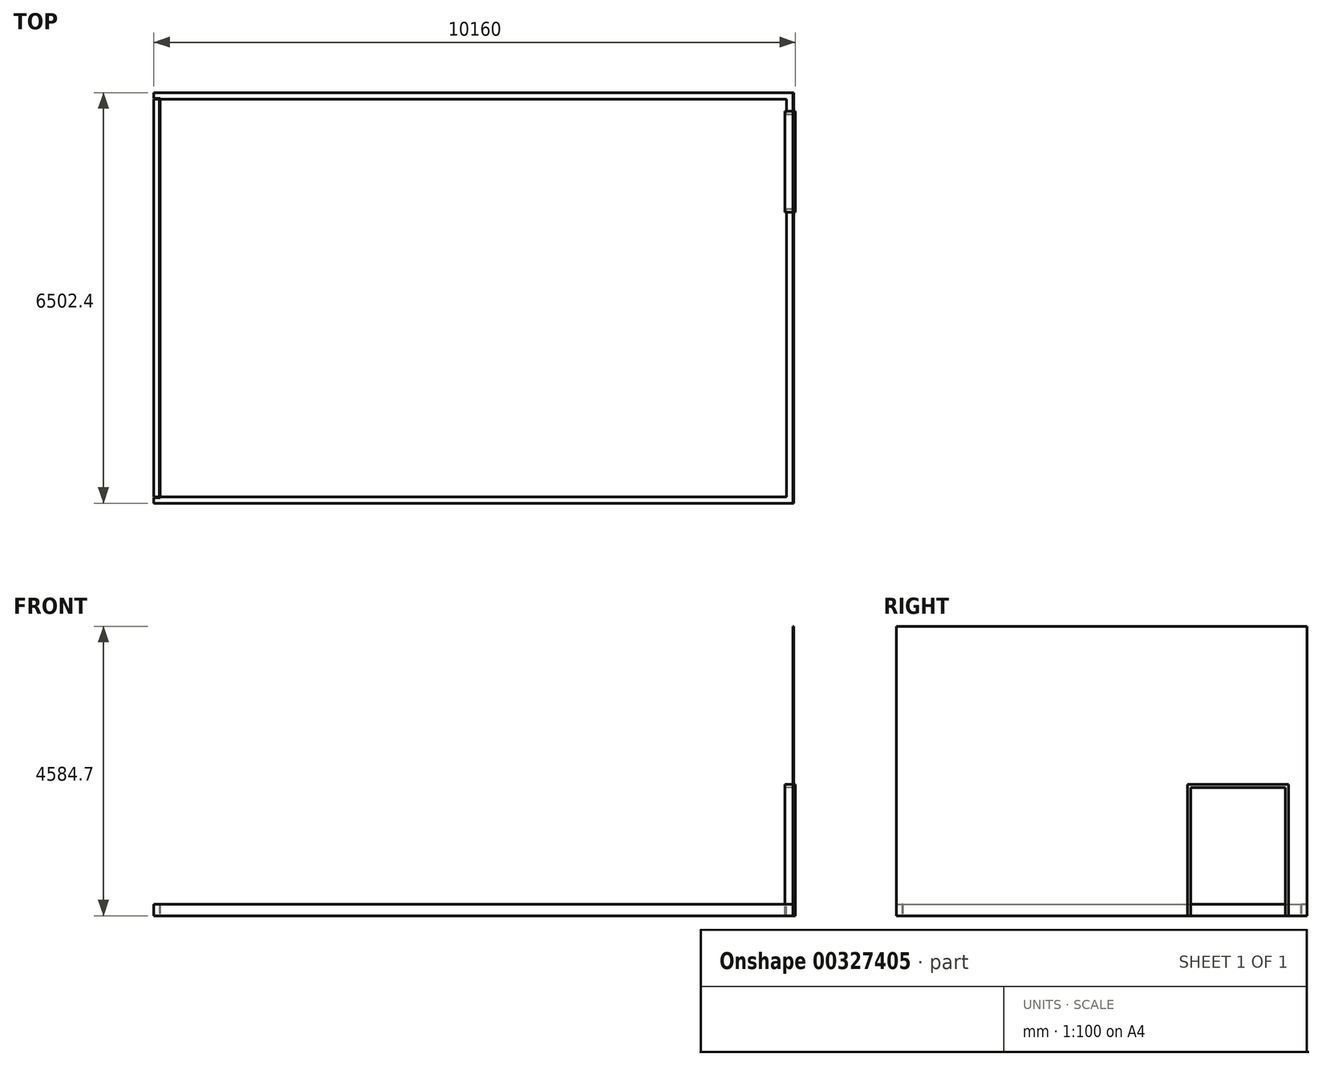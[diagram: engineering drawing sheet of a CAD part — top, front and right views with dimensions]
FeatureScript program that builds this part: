
annotation { "Feature Type Name" : "Feature", "Feature Type Description" : "" }
export const myFeature = defineFeature(function(context is Context, id is Id, definition is map)
    precondition{}
    {
        {
            assignVariable(context, id + "F0", {"name" : "WallHeight", "anyValue" : 15 * 12 + 0.5});
        }
        {
            var Q0;
            Q0=qCreatedBy(makeId("Top.planeOp"),FACE);
            var sketch = newSketch(context, id + "F1", { "sketchPlane" : qUnion([Q0])});
            skLineSegment(sketch, "E0.bottom", {"start": v(0, 6299.2) * mm, "end": v(9918.7, 6299.2) * mm});
            skLineSegment(sketch, "E0.top", {"start": v(0, 0) * mm, "end": v(9918.7, 0) * mm});
            skLineSegment(sketch, "E0.left", {"start": v(0, 6299.2) * mm, "end": v(0, 0) * mm});
            skLineSegment(sketch, "E0.right", {"start": v(9918.7, 6299.2) * mm, "end": v(9918.7, 0) * mm});
            skSolve(sketch);
        }
        {
            var Q0;
            Q0=qCreatedBy(makeId("Top.planeOp"),FACE);
            var sketch = newSketch(context, id + "F2", { "sketchPlane" : qUnion([Q0])});
            skLineSegment(sketch, "E1.bottom", {"start": v(0, 0) * mm, "end": v(-12.7, 0) * mm});
            skLineSegment(sketch, "E1.top", {"start": v(0, 6299.2) * mm, "end": v(-12.7, 6299.2) * mm});
            skLineSegment(sketch, "E1.left", {"start": v(0, 0) * mm, "end": v(0, 6299.2) * mm});
            skLineSegment(sketch, "E1.right", {"start": v(-12.7, 0) * mm, "end": v(-12.7, 6299.2) * mm});
            skSolve(sketch);
        }
        {
            var Q0;
            Q0=makeQuery(id+"F2.imprint","IMPRINT",FACE,{"disambiguationData":[TD([[makeQuery(id+"F2.imprint","IMPRINT",EDGE,{"derivedFrom":sQuery(id+"F2.wireOp",EDGE,"E1.bottom")}),-1.0]])]});
            extrude(context, id + "F3", {"entities" : qUnion([Q0]), "depth" : (getVariable(context, 'WallHeight')) * mm});
        }
        {
            var Q0;
            Q0=qCreatedBy(makeId("Top.planeOp"),FACE);
            var sketch = newSketch(context, id + "F4", { "sketchPlane" : qUnion([Q0])});
            skLineSegment(sketch, "E2.bottom", {"start": v(0, 0) * mm, "end": v(9918.7, 0) * mm});
            skLineSegment(sketch, "E2.top", {"start": v(0, -12.7) * mm, "end": v(9918.7, -12.7) * mm});
            skLineSegment(sketch, "E2.left", {"start": v(0, 0) * mm, "end": v(0, -12.7) * mm});
            skLineSegment(sketch, "E2.right", {"start": v(9918.7, 0) * mm, "end": v(9918.7, -12.7) * mm});
            skSolve(sketch);
        }
        {
            var Q0;
            Q0=qSketchRegion(id+"F4",true);
            extrude(context, id + "F5", {"entities" : qUnion([Q0]), "depth" : (getVariable(context, 'WallHeight')) * mm});
        }
        {
            var Q0;
            Q0=qCreatedBy(makeId("Top.planeOp"),FACE);
            var sketch = newSketch(context, id + "F6", { "sketchPlane" : qUnion([Q0])});
            skLineSegment(sketch, "E3.bottom", {"start": v(9918.7, 0) * mm, "end": v(9931.4, 0) * mm});
            skLineSegment(sketch, "E3.top", {"start": v(9918.7, 6299.2) * mm, "end": v(9931.4, 6299.2) * mm});
            skLineSegment(sketch, "E3.left", {"start": v(9918.7, 0) * mm, "end": v(9918.7, 6299.2) * mm});
            skLineSegment(sketch, "E3.right", {"start": v(9931.4, 0) * mm, "end": v(9931.4, 6299.2) * mm});
            skSolve(sketch);
        }
        {
            var Q0;
            Q0=qSketchRegion(id+"F6",true);
            extrude(context, id + "F7", {"entities" : qUnion([Q0]), "depth" : (getVariable(context, 'WallHeight')) * mm});
        }
        {
            var Q0;
            Q0=qCreatedBy(makeId("Top.planeOp"),FACE);
            var sketch = newSketch(context, id + "F8", { "sketchPlane" : qUnion([Q0])});
            skLineSegment(sketch, "E4.bottom", {"start": v(0, 6299.2) * mm, "end": v(9918.7, 6299.2) * mm});
            skLineSegment(sketch, "E4.top", {"start": v(0, 6311.9) * mm, "end": v(9918.7, 6311.9) * mm});
            skLineSegment(sketch, "E4.left", {"start": v(0, 6299.2) * mm, "end": v(0, 6311.9) * mm});
            skLineSegment(sketch, "E4.right", {"start": v(9918.7, 6299.2) * mm, "end": v(9918.7, 6311.9) * mm});
            skSolve(sketch);
        }
        {
            var Q0;
            Q0=qSketchRegion(id+"F8",true);
            extrude(context, id + "F9", {"entities" : qUnion([Q0]), "depth" : (getVariable(context, 'WallHeight')) * mm});
        }
        {
            var Q0;
            Q0=makeQuery(id+"F3.opExtrude","SWEPT_FACE",FACE,{"disambiguationData":[OSD([sQuery(id+"F2.wireOp",EDGE,"E1.right")])]});
            extrude(context, id + "F10", {"entities" : qUnion([Q0]), "depth" : 88.9 * mm});
        }
        {
            var Q0;
            Q0=makeQuery(id+"F7.opExtrude","SWEPT_FACE",FACE,{"disambiguationData":[OSD([sQuery(id+"F6.wireOp",EDGE,"E3.right")])]});
            extrude(context, id + "F11", {"entities" : qUnion([Q0]), "depth" : 88.9 * mm});
        }
        {
            var Q0;
            Q0=makeQuery(id+"F5.opExtrude","SWEPT_FACE",FACE,{"disambiguationData":[OSD([sQuery(id+"F4.wireOp",EDGE,"E2.top")])]});
            extrude(context, id + "F12", {"entities" : qUnion([Q0]), "depth" : 88.9 * mm});
        }
        {
            var Q0;
            Q0=makeQuery(id+"F12.opExtrude","SWEPT_FACE",FACE,{"disambiguationData":[OSD([sQuery(id+"F4.wireOp",EDGE,"E2.top"),sQuery(id+"F4.wireOp",EDGE,"E2.left")])]});
            extrude(context, id + "F13", {"entities" : qUnion([Q0]), "operationType" : NewBodyOperationType.ADD, "depth" : 101.6 * mm});
        }
        {
            var Q0;
            Q0=makeQuery(id+"F12.opExtrude","SWEPT_FACE",FACE,{"disambiguationData":[OSD([sQuery(id+"F4.wireOp",EDGE,"E2.top"),sQuery(id+"F4.wireOp",EDGE,"E2.right")])]});
            extrude(context, id + "F14", {"entities" : qUnion([Q0]), "operationType" : NewBodyOperationType.ADD, "depth" : 101.6 * mm});
        }
        {
            var Q0;
            Q0=makeQuery(id+"F9.opExtrude","SWEPT_FACE",FACE,{"disambiguationData":[OSD([sQuery(id+"F8.wireOp",EDGE,"E4.top")])]});
            extrude(context, id + "F15", {"entities" : qUnion([Q0]), "depth" : 88.9 * mm});
        }
        {
            var Q0;
            Q0=makeQuery(id+"F15.opExtrude","SWEPT_FACE",FACE,{"disambiguationData":[OSD([sQuery(id+"F8.wireOp",EDGE,"E4.top"),sQuery(id+"F8.wireOp",EDGE,"E4.left")])]});
            extrude(context, id + "F16", {"entities" : qUnion([Q0]), "operationType" : NewBodyOperationType.ADD, "depth" : 101.6 * mm});
        }
        {
            var Q0;
            Q0=makeQuery(id+"F15.opExtrude","SWEPT_FACE",FACE,{"disambiguationData":[OSD([sQuery(id+"F8.wireOp",EDGE,"E4.top"),sQuery(id+"F8.wireOp",EDGE,"E4.right")])]});
            extrude(context, id + "F17", {"entities" : qUnion([Q0]), "operationType" : NewBodyOperationType.ADD, "depth" : 101.6 * mm});
        }
        {
            var Q0;
            Q0=makeQuery(id+"F11.opExtrude","CAP_FACE",FACE,{"disambiguationData":[OSD([sQuery(id+"F6.wireOp",EDGE,"E3.right")])],"isStart":false});
            var sketch = newSketch(context, id + "F18", { "sketchPlane" : qUnion([Q0])});
            skLineSegment(sketch, "E5.bottom", {"start": v(-101.6, 4584.7) * mm, "end": v(6400.8, 4584.7) * mm});
            skLineSegment(sketch, "E5.top", {"start": v(-101.6, 0) * mm, "end": v(6400.8, 0) * mm});
            skLineSegment(sketch, "E5.left", {"start": v(6400.8, 4584.7) * mm, "end": v(6400.8, 0) * mm});
            skLineSegment(sketch, "E5.right", {"start": v(-101.6, 4584.7) * mm, "end": v(-101.6, 0) * mm});
            skSolve(sketch);
        }
        {
            var Q0;
            Q0=qSketchRegion(id+"F18",true);
            extrude(context, id + "F19", {"entities" : qUnion([Q0]), "depth" : 12.7 * mm});
        }
        {
            var Q0;
            Q0=makeQuery(id+"F7.opExtrude","SWEPT_FACE",FACE,{"disambiguationData":[OSD([sQuery(id+"F6.wireOp",EDGE,"E3.left")])]});
            var sketch = newSketch(context, id + "F20", { "sketchPlane" : qUnion([Q0])});
            skLineSegment(sketch, "E6.bottom", {"start": v(-6108.7, 0) * mm, "end": v(-4508.5, 0) * mm});
            skLineSegment(sketch, "E6.top", {"start": v(-6108.7, 2082.8) * mm, "end": v(-4508.5, 2082.8) * mm});
            skLineSegment(sketch, "E6.left", {"start": v(-6108.7, 0) * mm, "end": v(-6108.7, 2082.8) * mm});
            skLineSegment(sketch, "E6.right", {"start": v(-4508.5, 0) * mm, "end": v(-4508.5, 2082.8) * mm});
            skSolve(sketch);
        }
        {
            var Q0;
            Q0=qSketchRegion(id+"F20",true);
            extrude(context, id + "F21", {"entities" : qUnion([Q0]), "depth" : 25.4 * mm, "hasSecondDirection" : true, "secondDirectionOppositeDirection" : true, "secondDirectionDepth" : 139.7 * mm});
        }
        {
            var Q0;
            Q0=makeQuery(id+"F21.opExtrude","CAP_FACE",FACE,{"disambiguationData":[OSD([sQuery(id+"F20.wireOp",EDGE,"E6.bottom"),sQuery(id+"F20.wireOp",EDGE,"E6.top"),sQuery(id+"F20.wireOp",EDGE,"E6.left"),sQuery(id+"F20.wireOp",EDGE,"E6.right")])],"isStart":false});
            var sketch = newSketch(context, id + "F22", { "sketchPlane" : qUnion([Q0])});
            skLineSegment(sketch, "E7.bottom", {"start": v(-6057.9, 0) * mm, "end": v(-4559.3, 0) * mm});
            skLineSegment(sketch, "E7.top", {"start": v(-6057.9, 2032) * mm, "end": v(-4559.3, 2032) * mm});
            skLineSegment(sketch, "E7.left", {"start": v(-6057.9, 0) * mm, "end": v(-6057.9, 2032) * mm});
            skLineSegment(sketch, "E7.right", {"start": v(-4559.3, 0) * mm, "end": v(-4559.3, 2032) * mm});
            skSolve(sketch);
        }
        {
            var Q0;
            Q0=qSketchRegion(id+"F22",true);
            var Q1;
            Q1=makeQuery(id+"F21.opExtrude","CAP_FACE",FACE,{"disambiguationData":[OSD([sQuery(id+"F20.wireOp",EDGE,"E6.bottom"),sQuery(id+"F20.wireOp",EDGE,"E6.top"),sQuery(id+"F20.wireOp",EDGE,"E6.left"),sQuery(id+"F20.wireOp",EDGE,"E6.right")])],"isStart":true});
            extrude(context, id + "F23", {"entities" : qUnion([Q0]), "operationType" : NewBodyOperationType.REMOVE, "endBound" : BoundingType.UP_TO_SURFACE, "oppositeDirection" : true, "endBoundEntityFace" : qUnion([Q1]), "offsetDistance" : 25.4 * mm, "depth" : 25.4 * mm});
        }
    });
